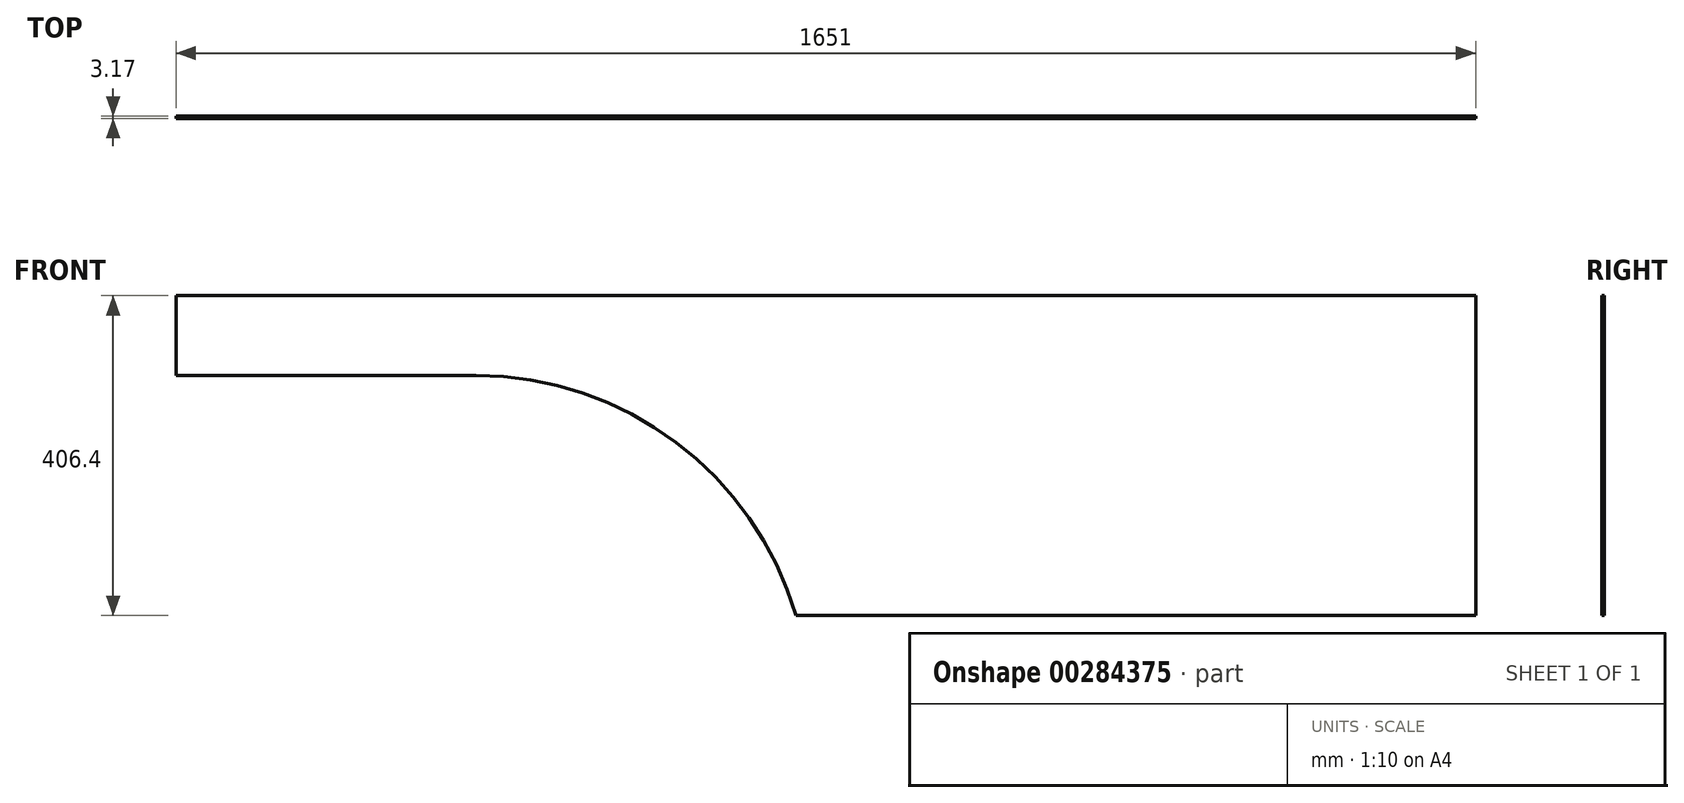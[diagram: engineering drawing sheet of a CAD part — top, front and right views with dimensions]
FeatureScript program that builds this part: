
annotation { "Feature Type Name" : "Feature", "Feature Type Description" : "" }
export const myFeature = defineFeature(function(context is Context, id is Id, definition is map)
    precondition{}
    {
        {
            var Q0;
            Q0=qCreatedBy(makeId("Front.planeOp"),FACE);
            var sketch = newSketch(context, id + "F0", { "sketchPlane" : qUnion([Q0])});
            skLineSegment(sketch, "E0", {"start": v(0, 52.72) * mm, "end": v(1651, 52.72) * mm});
            skLineSegment(sketch, "E1", {"start": v(1651, 52.72) * mm, "end": v(1651, -353.68) * mm});
            skLineSegment(sketch, "E2", {"start": v(1651, -353.68) * mm, "end": v(787.4, -353.68) * mm});
            skLineSegment(sketch, "E3", {"start": v(381, -48.88) * mm, "end": v(0, -48.88) * mm});
            skLineSegment(sketch, "E4", {"start": v(0, -48.88) * mm, "end": v(0, 52.72) * mm});
            skArc(sketch, "E5", {"start": v(787.4, -353.68) * mm, "mid": v(635, -133.55) * mm, "end": v(381, -48.88) * mm});
            skSolve(sketch);
        }
        {
            var Q0;
            Q0 = qSketchRegion(id + "F0", true);
            extrude(context, id + "F1", {"entities" : qUnion([Q0]), "depth" : 3.17 * mm});
        }
    });
